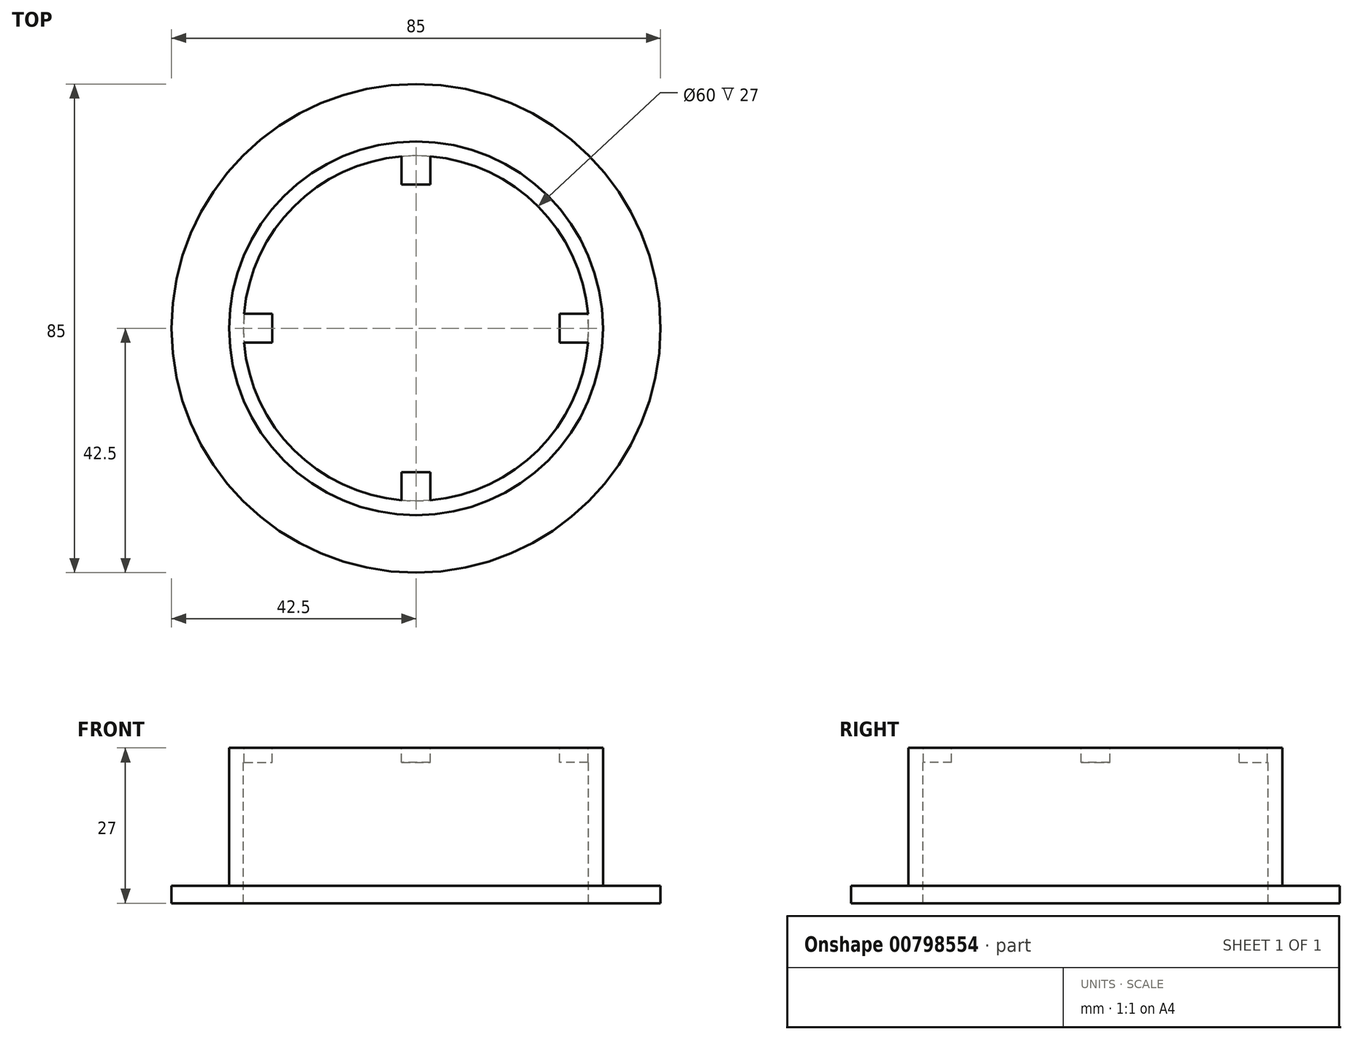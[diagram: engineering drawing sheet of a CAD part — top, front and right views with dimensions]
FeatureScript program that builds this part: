
annotation { "Feature Type Name" : "Feature", "Feature Type Description" : "" }
export const myFeature = defineFeature(function(context is Context, id is Id, definition is map)
    precondition{}
    {
        {
            var Q0;
            Q0=qCreatedBy(makeId("Top.planeOp"),FACE);
            var sketch = newSketch(context, id + "F0", { "sketchPlane" : qUnion([Q0])});
            skCircle(sketch, "E0", {"center": v(0, 0) * mm, "radius": 32.5 * mm});
            skCircle(sketch, "E1", {"center": v(0, 0) * mm, "radius": 42.5 * mm});
            skCircle(sketch, "E2", {"center": v(0, 0) * mm, "radius": 30 * mm});
            skSolve(sketch);
        }
        {
            var Q0;
            Q0=makeQuery(id+"F0.imprint","IMPRINT",FACE,{"disambiguationData":[TD([[makeQuery(id+"F0.imprint","IMPRINT",EDGE,{"derivedFrom":sQuery(id+"F0.wireOp",EDGE,"E0")}),-1.0]])]});
            var Q1;
            Q1=makeQuery(id+"F0.imprint","IMPRINT",FACE,{"disambiguationData":[TD([[makeQuery(id+"F0.imprint","IMPRINT",EDGE,{"derivedFrom":sQuery(id+"F0.wireOp",EDGE,"E0")}),1.0]])]});
            extrude(context, id + "F1", {"entities" : qUnion([Q0, Q1]), "oppositeDirection" : true, "depth" : 3 * mm, "offsetDistance" : 25 * mm});
        }
        {
            var Q0;
            Q0=makeQuery(id+"F0.imprint","IMPRINT",FACE,{"disambiguationData":[TD([[makeQuery(id+"F0.imprint","IMPRINT",EDGE,{"derivedFrom":sQuery(id+"F0.wireOp",EDGE,"E0")}),1.0]])]});
            extrude(context, id + "F2", {"entities" : qUnion([Q0]), "operationType" : NewBodyOperationType.ADD, "depth" : 24 * mm, "offsetDistance" : 25 * mm});
        }
        {
            var Q0;
            Q0=makeQuery(id+"F2.opExtrude","CAP_FACE",FACE,{"disambiguationData":[OSD([sQuery(id+"F0.wireOp",EDGE,"E0"),sQuery(id+"F0.wireOp",EDGE,"E2")])],"isStart":false});
            var sketch = newSketch(context, id + "F3", { "sketchPlane" : qUnion([Q0])});
            skLineSegment(sketch, "E3", {"start": v(0, 30) * mm, "end": v(0, -32.5) * mm, "construction": true});
            skLineSegment(sketch, "E4.bottom", {"start": v(30, -2.5) * mm, "end": v(25, -2.5) * mm});
            skLineSegment(sketch, "E4.top", {"start": v(30, 2.5) * mm, "end": v(25, 2.5) * mm});
            skLineSegment(sketch, "E4.left", {"start": v(30, -2.5) * mm, "end": v(30, 2.5) * mm});
            skLineSegment(sketch, "E4.right", {"start": v(25, -2.5) * mm, "end": v(25, 2.5) * mm});
            skPoint(sketch, "E4.middle", {"position": v(27.5, 0) * mm});
            skLineSegment(sketch, "E5.MirrorCS", {"start": v(-30, 2.5) * mm, "end": v(-25, 2.5) * mm});
            skLineSegment(sketch, "E6.MirrorCS", {"start": v(-25, -2.5) * mm, "end": v(-25, 2.5) * mm});
            skLineSegment(sketch, "E7.MirrorCS", {"start": v(-30, -2.5) * mm, "end": v(-25, -2.5) * mm});
            skLineSegment(sketch, "E8.MirrorCS", {"start": v(-30, -2.5) * mm, "end": v(-30, 2.5) * mm});
            skPoint(sketch, "E9.middle", {"position": v(0, 31.25) * mm});
            skLineSegment(sketch, "E10.bottom", {"start": v(2.5, 25) * mm, "end": v(-2.5, 25) * mm});
            skLineSegment(sketch, "E10.top", {"start": v(2.5, 30) * mm, "end": v(-2.5, 30) * mm});
            skLineSegment(sketch, "E10.left", {"start": v(2.5, 25) * mm, "end": v(2.5, 30) * mm});
            skLineSegment(sketch, "E10.right", {"start": v(-2.5, 25) * mm, "end": v(-2.5, 30) * mm});
            skPoint(sketch, "E10.middle", {"position": v(0, 27.5) * mm});
            skLineSegment(sketch, "E11", {"start": v(-32.5, 0) * mm, "end": v(32.5, 0) * mm, "construction": true});
            skPoint(sketch, "E11.startSnap0", {"position": v(-30, 0) * mm});
            skPoint(sketch, "E11.endSnap0", {"position": v(30, 0) * mm});
            skLineSegment(sketch, "E12.MirrorCS", {"start": v(-2.5, -25) * mm, "end": v(-2.5, -30) * mm});
            skLineSegment(sketch, "E13.MirrorCS", {"start": v(2.5, -30) * mm, "end": v(-2.5, -30) * mm});
            skLineSegment(sketch, "E14.MirrorCS", {"start": v(2.5, -25) * mm, "end": v(2.5, -30) * mm});
            skLineSegment(sketch, "E15.MirrorCS", {"start": v(2.5, -25) * mm, "end": v(-2.5, -25) * mm});
            skSolve(sketch);
        }
        {
            var Q0;
            {var subQ4=sQuery(id+"F3.wireOp",EDGE,"E4.right");Q0=makeQuery(id+"F3.imprint","IMPRINT",FACE,{"disambiguationData":[TD([[makeQuery(id+"F3.imprint","IMPRINT",EDGE,{"derivedFrom":subQ4}),-1.0]])]});}
            var Q1;
            {var subQ1=sQuery(id+"F3.wireOp",EDGE,"E6.MirrorCS");Q1=makeQuery(id+"F3.imprint","IMPRINT",FACE,{"disambiguationData":[TD([[makeQuery(id+"F3.imprint","IMPRINT",EDGE,{"derivedFrom":subQ1}),1.0]])]});}
            var Q2;
            {var subQ4=sQuery(id+"F3.wireOp",EDGE,"E10.bottom");Q2=makeQuery(id+"F3.imprint","IMPRINT",FACE,{"disambiguationData":[TD([[makeQuery(id+"F3.imprint","IMPRINT",EDGE,{"derivedFrom":subQ4}),-1.0]])]});}
            var Q3;
            {var subQ4=sQuery(id+"F3.wireOp",EDGE,"E15.MirrorCS");Q3=makeQuery(id+"F3.imprint","IMPRINT",FACE,{"disambiguationData":[TD([[makeQuery(id+"F3.imprint","IMPRINT",EDGE,{"derivedFrom":subQ4}),1.0]])]});}
            extrude(context, id + "F4", {"entities" : qUnion([Q0, Q1, Q2, Q3]), "operationType" : NewBodyOperationType.ADD, "oppositeDirection" : true, "depth" : 2.5 * mm, "offsetDistance" : 25 * mm});
        }
    });
